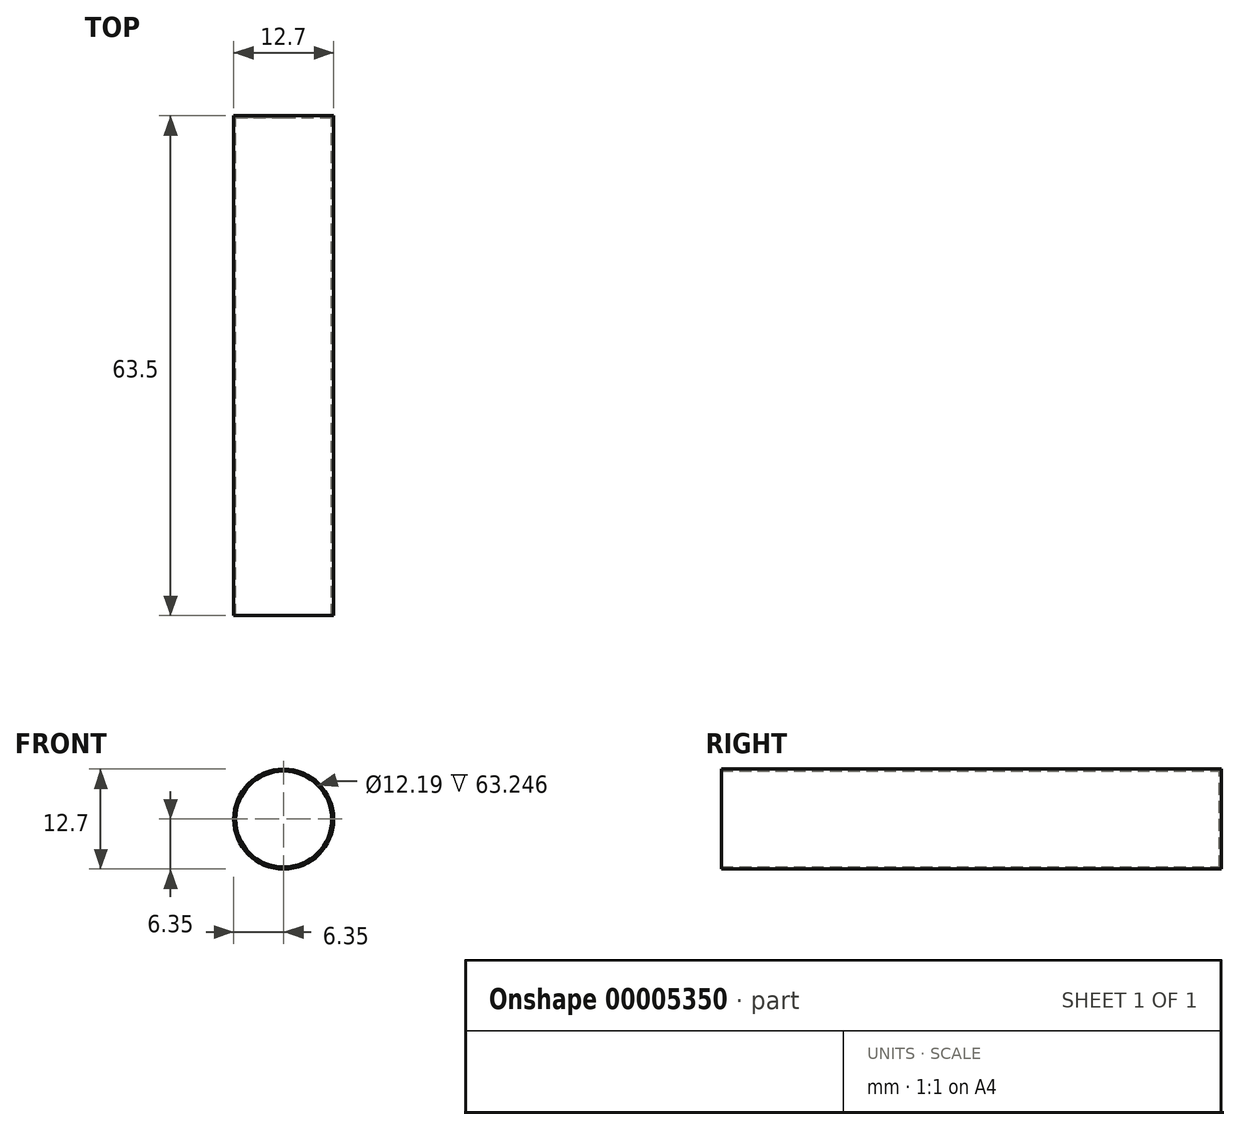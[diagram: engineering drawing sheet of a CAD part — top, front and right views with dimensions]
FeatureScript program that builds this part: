
annotation { "Feature Type Name" : "Feature", "Feature Type Description" : "" }
export const myFeature = defineFeature(function(context is Context, id is Id, definition is map)
    precondition{}
    {
        {
            var Q0;
            Q0=qCreatedBy(makeId("Front.planeOp"),FACE);
            var sketch = newSketch(context, id + "F0", { "sketchPlane" : qUnion([Q0])});
            skCircle(sketch, "E0", {"center": v(0, 0) * mm, "radius": 6.35 * mm});
            skSolve(sketch);
        }
        {
            var Q0;
            Q0 = qSketchRegion(id + "F0", true);
            extrude(context, id + "F1", {"entities" : qUnion([Q0]), "flatOperationType" : FlatOperationType.REMOVE, "depth" : 63.5 * mm, "offsetDistance" : 25.4 * mm, "domain" : OperationDomain.MODEL});
        }
        {
            var Q0;
            Q0=makeQuery(id+"F1.opExtrude","CAP_FACE",FACE,{"disambiguationData":[OSD([sQuery(id+"F0.wireOp",EDGE,"E0")])],"isStart":false});
            shell(context, id + "F2", {"entities" : qUnion([Q0]), "thickness" : 0.25 * mm});
        }
    });
